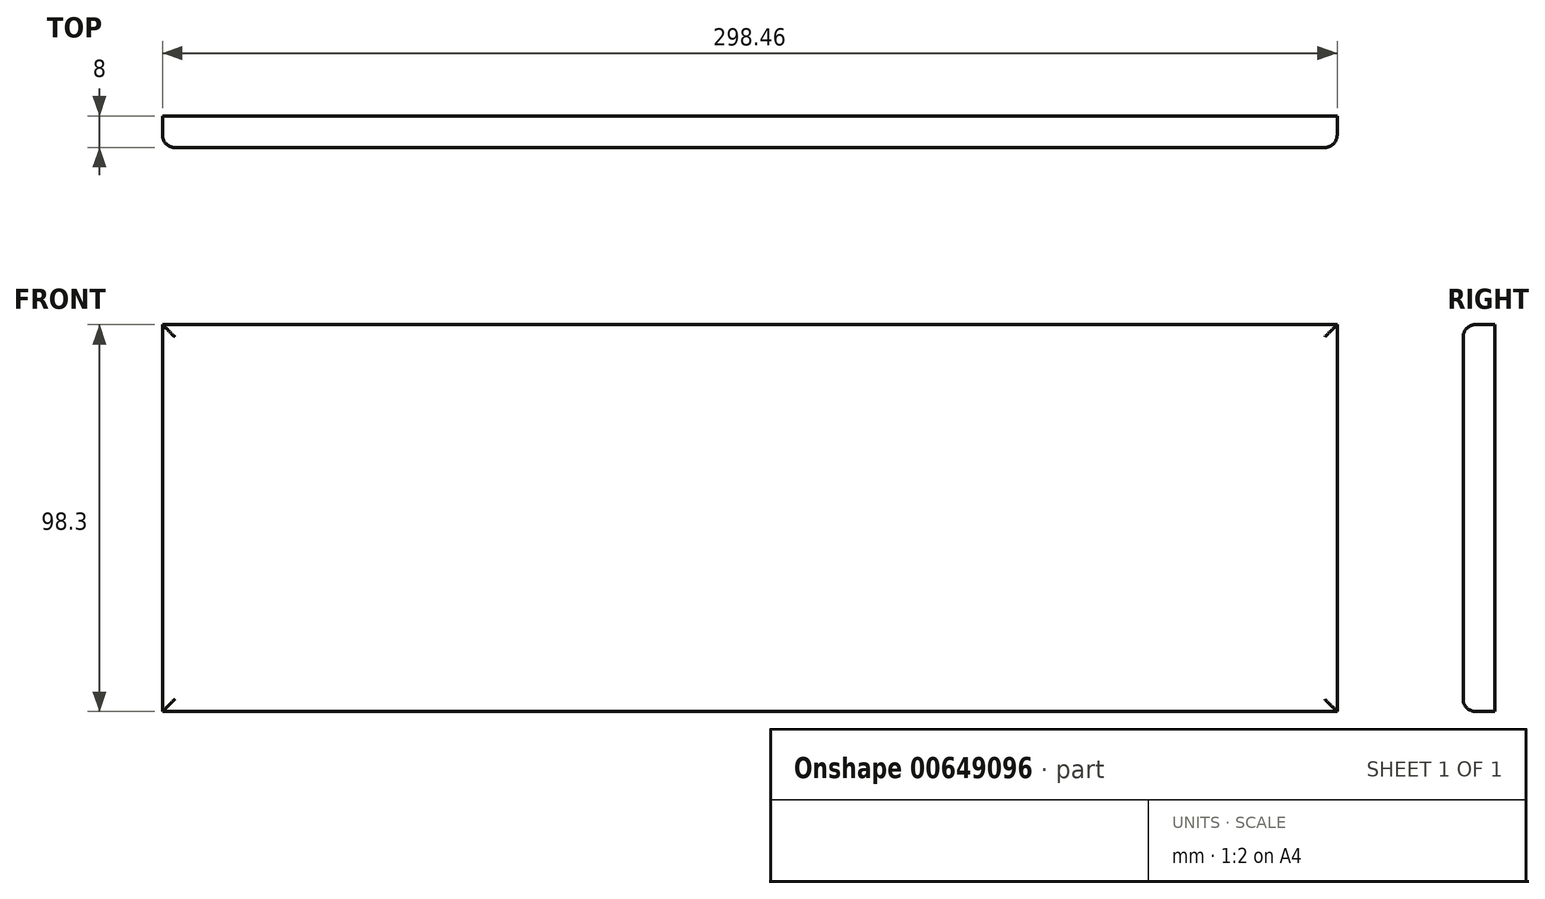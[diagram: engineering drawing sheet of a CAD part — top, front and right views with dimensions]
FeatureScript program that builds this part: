
annotation { "Feature Type Name" : "Feature", "Feature Type Description" : "" }
export const myFeature = defineFeature(function(context is Context, id is Id, definition is map)
    precondition{}
    {
        {
            var Q0;
            Q0=qCreatedBy(makeId("Front.planeOp"),FACE);
            var sketch = newSketch(context, id + "F0", { "sketchPlane" : qUnion([Q0])});
            skLineSegment(sketch, "E0.bottom", {"start": v(149.23, 49.15) * mm, "end": v(-149.23, 49.15) * mm});
            skLineSegment(sketch, "E0.top", {"start": v(149.23, -49.15) * mm, "end": v(-149.23, -49.15) * mm});
            skLineSegment(sketch, "E0.left", {"start": v(149.23, 49.15) * mm, "end": v(149.23, -49.15) * mm});
            skLineSegment(sketch, "E0.right", {"start": v(-149.23, 49.15) * mm, "end": v(-149.23, -49.15) * mm});
            skPoint(sketch, "E0.middle", {"position": v(0, 0) * mm});
            skSolve(sketch);
        }
        {
            var Q0;
            Q0 = qSketchRegion(id + "F0", true);
            extrude(context, id + "F1", {"entities" : qUnion([Q0]), "depth" : 8 * mm, "offsetDistance" : 25.4 * mm});
        }
        {
            var Q0;
            Q0=makeQuery(id+"F1.opExtrude","CAP_FACE",FACE,{"disambiguationData":[OSD([sQuery(id+"F0.wireOp",EDGE,"E0.bottom"),sQuery(id+"F0.wireOp",EDGE,"E0.top"),sQuery(id+"F0.wireOp",EDGE,"E0.left"),sQuery(id+"F0.wireOp",EDGE,"E0.right")])],"isStart":false});
            fillet(context, id + "F2", {"entities" : qUnion([Q0]), "radius" : 3.17 * mm, "tangentPropagation" : true, "allowEdgeOverflow" : false});
        }
    });
